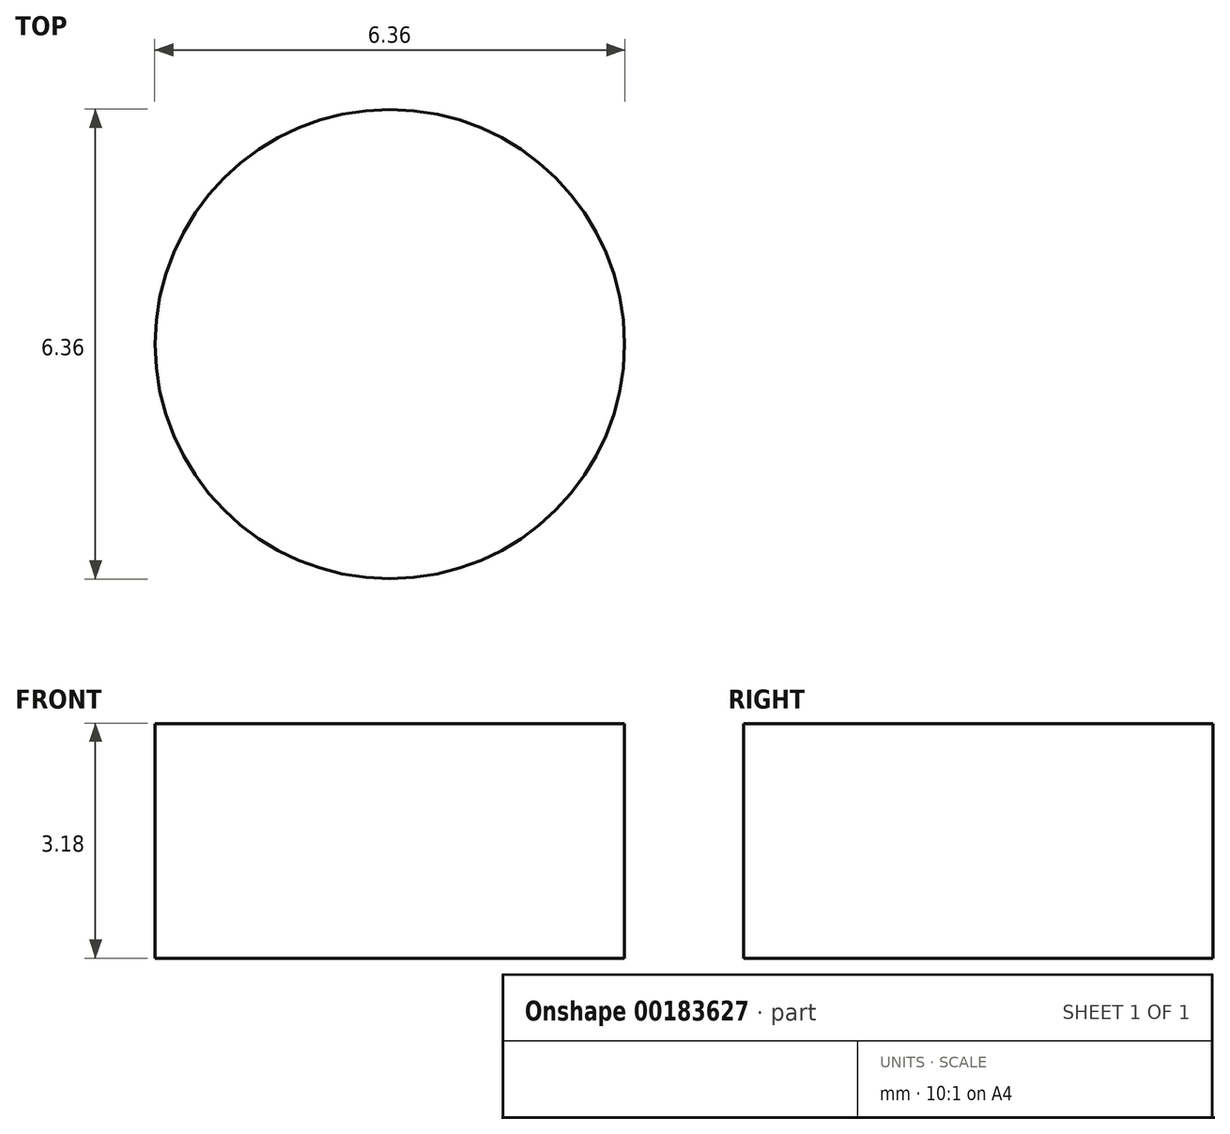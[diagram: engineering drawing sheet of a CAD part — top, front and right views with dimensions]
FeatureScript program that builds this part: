
annotation { "Feature Type Name" : "Feature", "Feature Type Description" : "" }
export const myFeature = defineFeature(function(context is Context, id is Id, definition is map)
    precondition{}
    {
        {
            var Q0;
            Q0=qCreatedBy(makeId("Top.planeOp"),FACE);
            var sketch = newSketch(context, id + "F0", { "sketchPlane" : qUnion([Q0])});
            skCircle(sketch, "E0", {"center": v(0, 0) * mm, "radius": 3.18 * mm});
            skSolve(sketch);
        }
        {
            var Q0;
            Q0=makeQuery(id+"F0.imprint","IMPRINT",FACE,{"disambiguationData":[TD([[makeQuery(id+"F0.imprint","IMPRINT",EDGE,{"derivedFrom":sQuery(id+"F0.wireOp",EDGE,"E0")}),1.0]])]});
            var sketch = newSketch(context, id + "F1", { "sketchPlane" : qUnion([Q0])});
            skCircle(sketch, "E1", {"center": v(0, 0) * mm, "radius": 1.59 * mm});
            skSolve(sketch);
        }
        {
            var Q0;
            Q0=sQuery(id+"F1.wireOp",EDGE,"E1");
            extrude(context, id + "F2", {"bodyType" : ToolBodyType.SURFACE, "surfaceEntities" : qUnion([Q0]), "depth" : 38.1 * mm});
        }
        {
            var Q0;
            Q0 = qSketchRegion(id + "F0", true);
            extrude(context, id + "F3", {"entities" : qUnion([Q0]), "depth" : 3.17 * mm});
        }
    });
